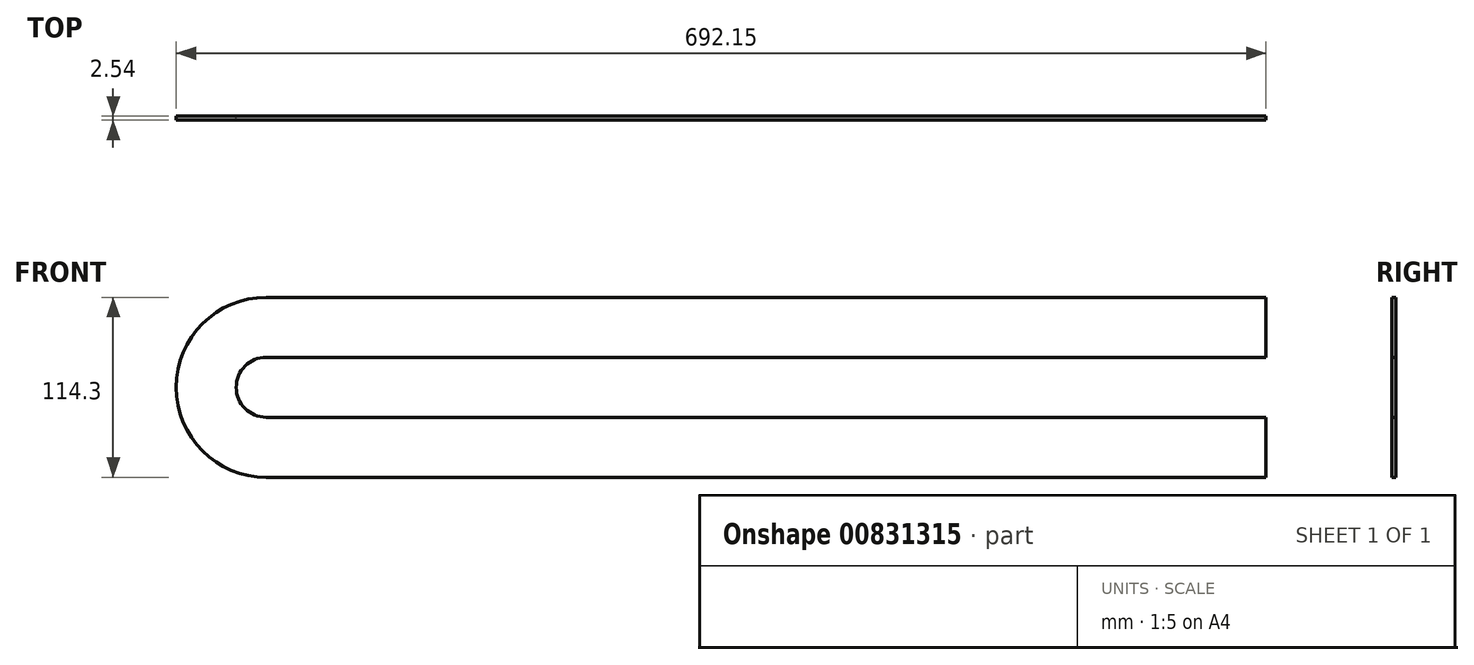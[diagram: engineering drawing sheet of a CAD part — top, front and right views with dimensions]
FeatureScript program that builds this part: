
annotation { "Feature Type Name" : "Feature", "Feature Type Description" : "" }
export const myFeature = defineFeature(function(context is Context, id is Id, definition is map)
    precondition{}
    {
        {
            var Q0;
            Q0=qCreatedBy(makeId("Front.planeOp"),FACE);
            var sketch = newSketch(context, id + "F0", { "sketchPlane" : qUnion([Q0])});
            skLineSegment(sketch, "E0.bottom", {"start": v(-83.04, 48.93) * mm, "end": v(551.96, 48.93) * mm});
            skLineSegment(sketch, "E0.top", {"start": v(-83.04, 10.83) * mm, "end": v(551.96, 10.83) * mm});
            skLineSegment(sketch, "E0.left", {"start": v(-83.04, 48.93) * mm, "end": v(-83.04, 10.83) * mm});
            skLineSegment(sketch, "E0.right", {"start": v(551.96, 48.93) * mm, "end": v(551.96, 10.83) * mm});
            skLineSegment(sketch, "E1.bottom", {"start": v(-83.04, -27.27) * mm, "end": v(551.96, -27.27) * mm});
            skLineSegment(sketch, "E1.top", {"start": v(-83.04, -65.37) * mm, "end": v(551.96, -65.37) * mm});
            skLineSegment(sketch, "E1.left", {"start": v(-83.04, -27.27) * mm, "end": v(-83.04, -65.37) * mm});
            skLineSegment(sketch, "E1.right", {"start": v(551.96, -27.27) * mm, "end": v(551.96, -65.37) * mm});
            skArc(sketch, "E2", {"start": v(-83.04, 10.83) * mm, "mid": v(-102.09, -8.22) * mm, "end": v(-83.04, -27.27) * mm});
            skArc(sketch, "E3", {"start": v(-83.04, 48.93) * mm, "mid": v(-140.19, -8.22) * mm, "end": v(-83.04, -65.37) * mm});
            skSolve(sketch);
        }
        {
            var Q0;
            Q0=makeQuery(id+"F0.imprint","IMPRINT",FACE,{"disambiguationData":[TD([[makeQuery(id+"F0.imprint","IMPRINT",EDGE,{"derivedFrom":sQuery(id+"F0.wireOp",EDGE,"E0.bottom")}),-1.0]])]});
            var Q1;
            Q1=makeQuery(id+"F0.imprint","IMPRINT",FACE,{"disambiguationData":[TD([[makeQuery(id+"F0.imprint","IMPRINT",EDGE,{"derivedFrom":sQuery(id+"F0.wireOp",EDGE,"E0.left")}),-1.0]])]});
            var Q2;
            Q2=makeQuery(id+"F0.imprint","IMPRINT",FACE,{"disambiguationData":[TD([[makeQuery(id+"F0.imprint","IMPRINT",EDGE,{"derivedFrom":sQuery(id+"F0.wireOp",EDGE,"E1.bottom")}),-1.0]])]});
            extrude(context, id + "F1", {"entities" : qUnion([Q0, Q1, Q2]), "depth" : 2.54 * mm, "offsetDistance" : 25.4 * mm});
        }
    });
